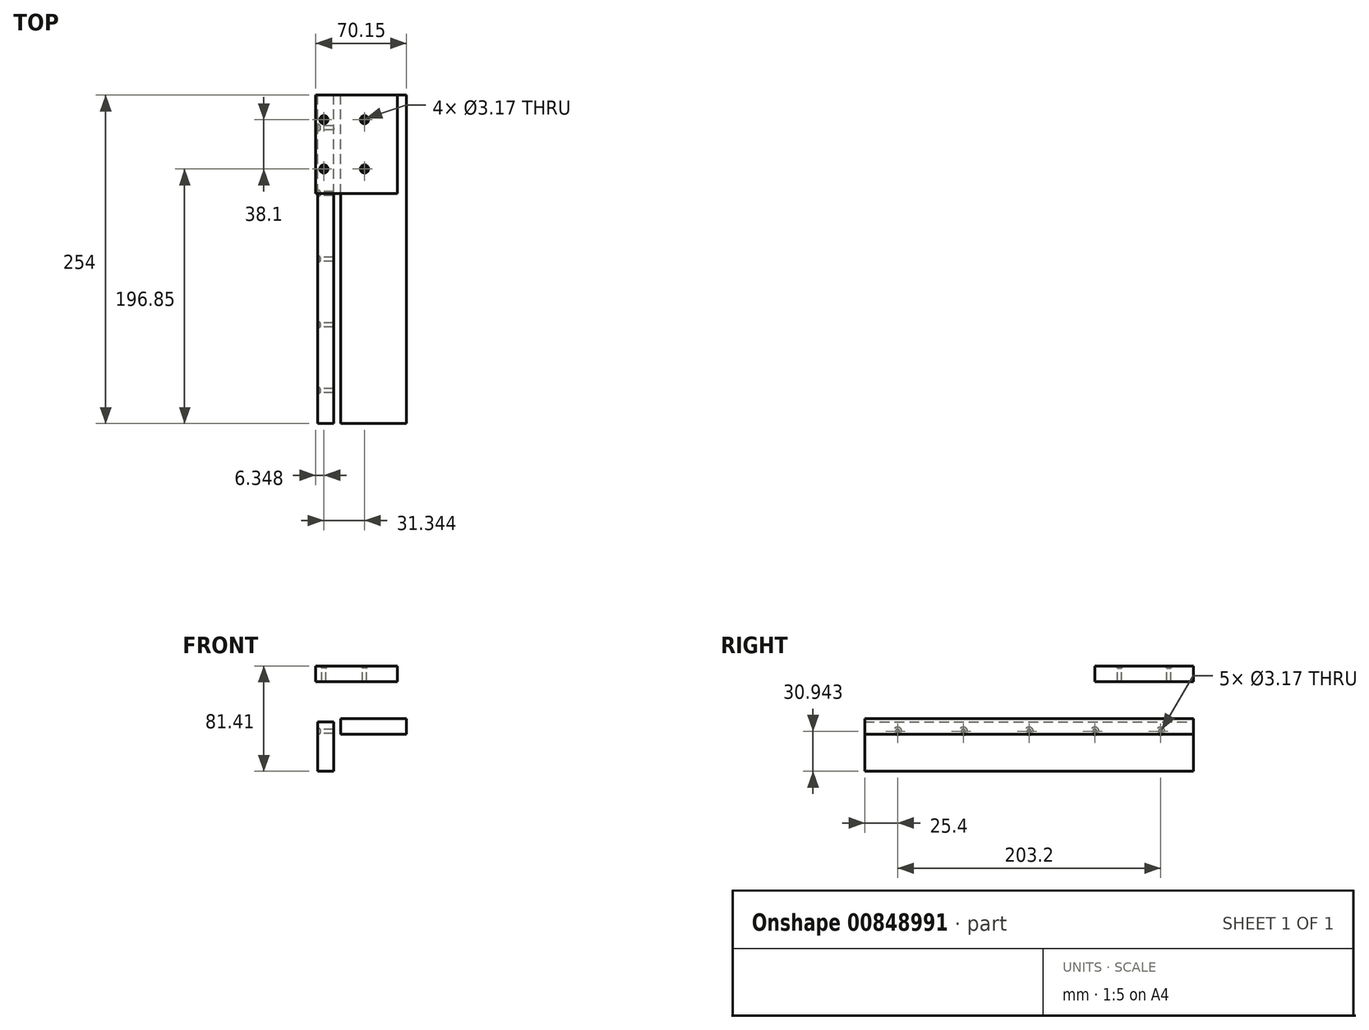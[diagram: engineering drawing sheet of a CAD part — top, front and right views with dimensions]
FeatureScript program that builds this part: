
annotation { "Feature Type Name" : "Feature", "Feature Type Description" : "" }
export const myFeature = defineFeature(function(context is Context, id is Id, definition is map)
    precondition{}
    {
        {
            var Q0;
            Q0=qCreatedBy(makeId("Front.planeOp"),FACE);
            var sketch = newSketch(context, id + "F0", { "sketchPlane" : qUnion([Q0])});
            skLineSegment(sketch, "E0.bottom", {"start": v(-40.46, -2.68) * mm, "end": v(-28.17, -2.68) * mm});
            skLineSegment(sketch, "E0.top", {"start": v(-40.46, -40.78) * mm, "end": v(-28.17, -40.78) * mm});
            skLineSegment(sketch, "E0.left", {"start": v(-40.46, -2.68) * mm, "end": v(-40.46, -40.78) * mm});
            skLineSegment(sketch, "E0.right", {"start": v(-28.17, -2.68) * mm, "end": v(-28.17, -40.78) * mm});
            skLineSegment(sketch, "E1.bottom", {"start": v(-22.64, 0) * mm, "end": v(28.16, 0) * mm});
            skLineSegment(sketch, "E1.top", {"start": v(-22.64, -12.3) * mm, "end": v(28.16, -12.3) * mm});
            skLineSegment(sketch, "E1.left", {"start": v(-22.64, 0) * mm, "end": v(-22.64, -12.3) * mm});
            skLineSegment(sketch, "E1.right", {"start": v(28.16, 0) * mm, "end": v(28.16, -12.3) * mm});
            skLineSegment(sketch, "E2.bottom", {"start": v(-42, 28.34) * mm, "end": v(21.1, 28.34) * mm});
            skLineSegment(sketch, "E2.top", {"start": v(-42, 40.63) * mm, "end": v(21.1, 40.63) * mm});
            skLineSegment(sketch, "E2.left", {"start": v(-42, 28.34) * mm, "end": v(-42, 40.63) * mm});
            skLineSegment(sketch, "E2.right", {"start": v(21.1, 28.34) * mm, "end": v(21.1, 40.63) * mm});
            skSolve(sketch);
        }
        {
            var Q0;
            Q0=makeQuery(id+"F0.imprint","IMPRINT",FACE,{"disambiguationData":[TD([[makeQuery(id+"F0.imprint","IMPRINT",EDGE,{"derivedFrom":sQuery(id+"F0.wireOp",EDGE,"E0.bottom")}),-1.0]])]});
            var Q1;
            Q1=makeQuery(id+"F0.imprint","IMPRINT",FACE,{"disambiguationData":[TD([[makeQuery(id+"F0.imprint","IMPRINT",EDGE,{"derivedFrom":sQuery(id+"F0.wireOp",EDGE,"E1.bottom")}),-1.0]])]});
            extrude(context, id + "F1", {"entities" : qUnion([Q0, Q1]), "depth" : 254 * mm, "offsetDistance" : 25.4 * mm});
        }
        {
            var Q0;
            Q0=makeQuery(id+"F0.imprint","IMPRINT",FACE,{"disambiguationData":[TD([[makeQuery(id+"F0.imprint","IMPRINT",EDGE,{"derivedFrom":sQuery(id+"F0.wireOp",EDGE,"E2.bottom")}),1.0]])]});
            extrude(context, id + "F2", {"entities" : qUnion([Q0]), "depth" : 76.2 * mm, "offsetDistance" : 25.4 * mm});
        }
        {
            var Q0;
            Q0=makeQuery(id+"F1.opExtrude","SWEPT_FACE",FACE,{"disambiguationData":[OSD([sQuery(id+"F0.wireOp",EDGE,"E0.left")])]});
            var sketch = newSketch(context, id + "F3", { "sketchPlane" : qUnion([Q0])});
            skPoint(sketch, "E3", {"position": v(25.4, -9.84) * mm});
            skPoint(sketch, "E4.1.0.0", {"position": v(76.2, -9.84) * mm});
            skPoint(sketch, "E4.2.0.0", {"position": v(127, -9.84) * mm});
            skPoint(sketch, "E4.3.0.0", {"position": v(177.8, -9.84) * mm});
            skPoint(sketch, "E4.4.0.0", {"position": v(228.6, -9.84) * mm});
            skLineSegment(sketch, "E4.direction1", {"start": v(25.4, -9.84) * mm, "end": v(76.2, -9.84) * mm, "construction": true});
            skSolve(sketch);
        }
        {
            var Q0;
            Q0=sQuery(id+"F3.wireOp",VERTEX,"E3");
            var Q1;
            Q1=sQuery(id+"F3.wireOp",VERTEX,"E4.1.0.0");
            var Q2;
            Q2=sQuery(id+"F3.wireOp",VERTEX,"E4.2.0.0");
            var Q3;
            Q3=sQuery(id+"F3.wireOp",VERTEX,"E4.3.0.0");
            var Q4;
            Q4=sQuery(id+"F3.wireOp",VERTEX,"E4.4.0.0");
            var Q5;
            Q5=makeQuery(id+"F1.opExtrude","SWEPT_BODY",BODY,{"disambiguationData":[OSD([sQuery(id+"F0.wireOp",EDGE,"E0.bottom"),sQuery(id+"F0.wireOp",EDGE,"E0.top"),sQuery(id+"F0.wireOp",EDGE,"E0.left"),sQuery(id+"F0.wireOp",EDGE,"E0.right")])]});
            hole(context, id + "F4", {"style" : HoleStyle.C_SINK, "endStyle" : HoleEndStyle.BLIND, "holeDiameter" : 3.17 * mm, "cSinkDiameter" : 6.35 * mm, "cSinkAngle" : 82 * degree, "majorDiameter" : 6.35 * mm, "holeDepth" : 12.7 * mm, "isTappedThrough" : true, "tappedDepth" : 12.7 * mm, "tapClearance" : 3, "startFromSketch" : true, "locations" : qUnion([Q0, Q1, Q2, Q3, Q4]), "scope" : qUnion([Q5])});
        }
        {
            var Q0;
            Q0=makeQuery(id+"F2.opExtrude","SWEPT_FACE",FACE,{"disambiguationData":[OSD([sQuery(id+"F0.wireOp",EDGE,"E2.top")])]});
            var sketch = newSketch(context, id + "F5", { "sketchPlane" : qUnion([Q0])});
            skPoint(sketch, "E5", {"position": v(-4.3, -19.05) * mm});
            skPoint(sketch, "E6", {"position": v(-4.3, -57.15) * mm});
            skPoint(sketch, "E7", {"position": v(-35.64, -19.05) * mm});
            skPoint(sketch, "E8", {"position": v(-35.64, -57.15) * mm});
            skSolve(sketch);
        }
        {
            var Q0;
            Q0=sQuery(id+"F5.wireOp",VERTEX,"E5");
            var Q1;
            Q1=sQuery(id+"F5.wireOp",VERTEX,"E6");
            var Q2;
            Q2=sQuery(id+"F5.wireOp",VERTEX,"E7");
            var Q3;
            Q3=sQuery(id+"F5.wireOp",VERTEX,"E8");
            var Q4;
            Q4=makeQuery(id+"F2.opExtrude","SWEPT_BODY",BODY,{"disambiguationData":[OSD([sQuery(id+"F0.wireOp",EDGE,"E2.bottom"),sQuery(id+"F0.wireOp",EDGE,"E2.top"),sQuery(id+"F0.wireOp",EDGE,"E2.left"),sQuery(id+"F0.wireOp",EDGE,"E2.right")])]});
            hole(context, id + "F6", {"style" : HoleStyle.C_SINK, "endStyle" : HoleEndStyle.BLIND, "holeDiameter" : 3.17 * mm, "cSinkDiameter" : 6.35 * mm, "cSinkAngle" : 82 * degree, "majorDiameter" : 6.35 * mm, "holeDepth" : 12.7 * mm, "isTappedThrough" : true, "tappedDepth" : 12.7 * mm, "tapClearance" : 3, "startFromSketch" : true, "locations" : qUnion([Q0, Q1, Q2, Q3]), "scope" : qUnion([Q4])});
        }
    });
